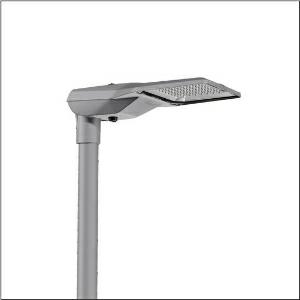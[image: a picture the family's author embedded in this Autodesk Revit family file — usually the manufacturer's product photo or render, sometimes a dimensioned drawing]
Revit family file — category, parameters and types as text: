
# Revit family: streetlight_sl_21_midi___p0_8ab_5xe3r33t08lb_8313
name_source: partatom
category: Lighting Fixtures
units: mm (PartAtom-declared; Revit-internal decimal feet)

## family parameters
Cut with Voids When Loaded = No
Host = Face
Light Source = No
Part Type = Normal
Room Calculation Point = No
Round Connector Dimension = Use Diameter
Shared = No

## types (1)
- --- (1 x LED, 12450 lm, 99.6 W, 3000K)
    Apparent Load = 100 VA
    CIE Flux Codes = 36 71 98 100 100
    Color Rendering = 70
    Color Temperature = 3000K
    Default Elevation = 1800 mm
    Description = Streetlight SL 21 midi, mast luminaire, primary light control with lens, of PMMA, primary optical cover: cover, of toughened safety glass, transparent, light distribution: P0.8aB, light emission: direct distribution, primary light characteristic: asymmetric, installation type: post-top, side-entry, LED, High Power LED, rated luminous flux: 12.450lm, luminous efficacy: 125lm/W, light colour: 730, colour temperature: 3000K, control gear: D4i, control: pre-setting: logarithmic dimming characteristic, flexible luminous flux parameterisation, time-dependent luminous flux control, constant luminous flux control, overheat protection, mains connection: 230..240V, AC, 50/60Hz, start of lifetime: 100W, end of service life: 102W, reduction: 46W, luminaire housing, of diecast aluminium, powder-coated, Siteco® metallic grey (DB 702S), corrosivity category C5 mid according to DIN EN ISO 12944, multi-level sealing system, sealing non-destructively replaceable, inclination adjustable: 0°, 5°, 10°, 15°, please order mast flange separately, length: 644mm, width: 335mm, height: 110mm, mast flange for spigot size: 42mm (side-entry): 5XC10008XM4, 60/48mm (side-entry/post-top): 5XC10108XM2, 76/60mm (side-entry/post-top): 5XC10108XM1, mounting height: 4..8m, Smart Interface below and above, protection rating (complete): IP66, insulation class (complete): insulation class II (safety insulation), certification: CE, ENEC, ENEC+, VDE, impact resistance: IK09, permissible operating ambient temperature for outdoor applications: -40..+50°C, standard-compliant lighting for roads and squares, packaging unit: 1 piece

Light Distribution: P0.8aB
    Height = 111 mm
    Lamp = 1 x LED
    Lamp Light Flux = 12450 lm
    Lamp Power = 99.6 W
    Lamp count = 1
    Length = 644 mm
    Luminous efficacy = 125 lm/W
    Manufacturer = Siteco
    ModVariant = No
    Model = 5XE3R33T08LB
    Number of Poles = 1
    OnlyDefault = Yes
    Power Factor = 1
    Product Name = Streetlight SL 21 midi | P0.8aB
    Product group = mast luminaire | pylon top
    ProductGroupID = 6100
    Protection Class = Protection class II
    Protection Degree = IP 66
    RLX_Detail_Level = 1
    RLX_Emergency_Light_Flux = 0 lm
    RLX_Emergency_Type = 0
    RLX_Emergency_Type_DB = No
    RlxData = <blob elided: 26553 chars, md5=c1147f5b>
    Socket = socket
    Standby Power = 0 W
    System Light Flux = 12450 lm
    System Power = 100 W
    Type Comments = factory setting: luminous flux: 100 % | dim-lin: 254 | 1020 mA
    Type Image = l_1004304.jpg
    URL = http://relux.com
    VarID = @adj_010229
    Voltage = 0 V
    Weight = 0.00 kg
    Width = 336 mm

## geometry (parser evidence)
native form markers: Blend x4, Sweep x10
no freeform markers — native parametric forms only
